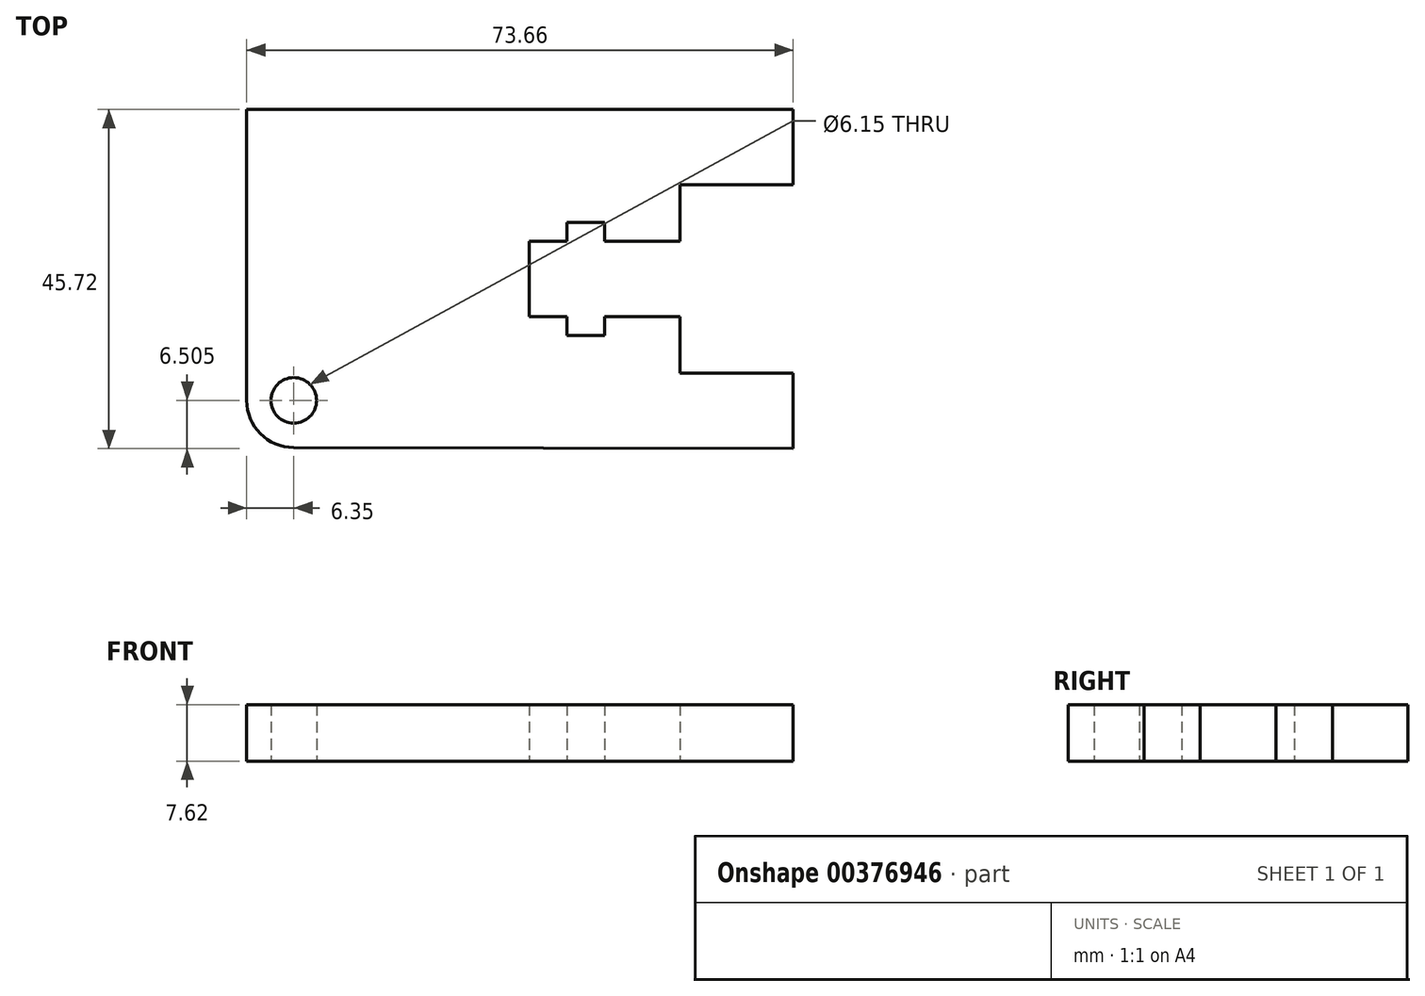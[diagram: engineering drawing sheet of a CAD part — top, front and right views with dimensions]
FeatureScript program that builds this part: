
annotation { "Feature Type Name" : "Feature", "Feature Type Description" : "" }
export const myFeature = defineFeature(function(context is Context, id is Id, definition is map)
    precondition{}
    {
        {
            var Q0;
            Q0=qCreatedBy(makeId("Top.planeOp"),FACE);
            var sketch = newSketch(context, id + "F0", { "sketchPlane" : qUnion([Q0])});
            skLineSegment(sketch, "E0", {"start": v(0, 0) * mm, "end": v(73.66, 0) * mm});
            skLineSegment(sketch, "E1", {"start": v(73.66, 0) * mm, "end": v(73.66, -10.16) * mm});
            skLineSegment(sketch, "E2.MirrorCS", {"start": v(73.66, 0) * mm, "end": v(73.66, 10.16) * mm});
            skLineSegment(sketch, "E3", {"start": v(73.66, -45.72) * mm, "end": v(73.66, -35.56) * mm});
            skLineSegment(sketch, "E4", {"start": v(73.66, -10.16) * mm, "end": v(58.42, -10.16) * mm});
            skLineSegment(sketch, "E5", {"start": v(73.66, -35.56) * mm, "end": v(58.42, -35.56) * mm});
            skLineSegment(sketch, "E6", {"start": v(58.42, -35.56) * mm, "end": v(58.42, -27.94) * mm});
            skLineSegment(sketch, "E7", {"start": v(58.42, -10.16) * mm, "end": v(58.42, -17.78) * mm});
            skLineSegment(sketch, "E8", {"start": v(58.42, -17.78) * mm, "end": v(48.26, -17.78) * mm});
            skLineSegment(sketch, "E9", {"start": v(58.42, -27.94) * mm, "end": v(48.26, -27.94) * mm});
            skLineSegment(sketch, "E10", {"start": v(48.26, -17.78) * mm, "end": v(48.26, -15.24) * mm});
            skLineSegment(sketch, "E11", {"start": v(48.26, -27.94) * mm, "end": v(48.26, -30.48) * mm});
            skLineSegment(sketch, "E12", {"start": v(48.26, -30.48) * mm, "end": v(43.18, -30.48) * mm});
            skLineSegment(sketch, "E13", {"start": v(48.26, -15.24) * mm, "end": v(43.18, -15.24) * mm});
            skLineSegment(sketch, "E14", {"start": v(43.18, -30.48) * mm, "end": v(43.18, -27.94) * mm});
            skLineSegment(sketch, "E15", {"start": v(43.18, -15.24) * mm, "end": v(43.18, -17.78) * mm});
            skLineSegment(sketch, "E16", {"start": v(43.18, -17.78) * mm, "end": v(38.1, -17.78) * mm});
            skLineSegment(sketch, "E17", {"start": v(43.18, -27.94) * mm, "end": v(38.1, -27.94) * mm});
            skLineSegment(sketch, "E18", {"start": v(38.1, -17.78) * mm, "end": v(38.1, -27.94) * mm});
            skLineSegment(sketch, "E19", {"start": v(0, 0) * mm, "end": v(0, -39.22) * mm});
            skLineSegment(sketch, "E20", {"start": v(6.34, -45.57) * mm, "end": v(73.66, -45.72) * mm});
            skPoint(sketch, "E21.visualSharp", {"position": v(0, -45.55) * mm});
            skArc(sketch, "E21.filletArc", {"start": v(0, -39.22) * mm, "mid": v(1.85, -43.7) * mm, "end": v(6.34, -45.57) * mm});
            skCircle(sketch, "E22", {"center": v(6.35, -39.22) * mm, "radius": 3.08 * mm});
            skSolve(sketch);
        }
        {
            var Q0;
            Q0=makeQuery(id+"F0.imprint","IMPRINT",FACE,{"disambiguationData":[TD([[makeQuery(id+"F0.imprint","IMPRINT",EDGE,{"derivedFrom":sQuery(id+"F0.wireOp",EDGE,"E0")}),-1.0]])]});
            extrude(context, id + "F1", {"entities" : qUnion([Q0]), "depth" : 7.62 * mm});
        }
    });
